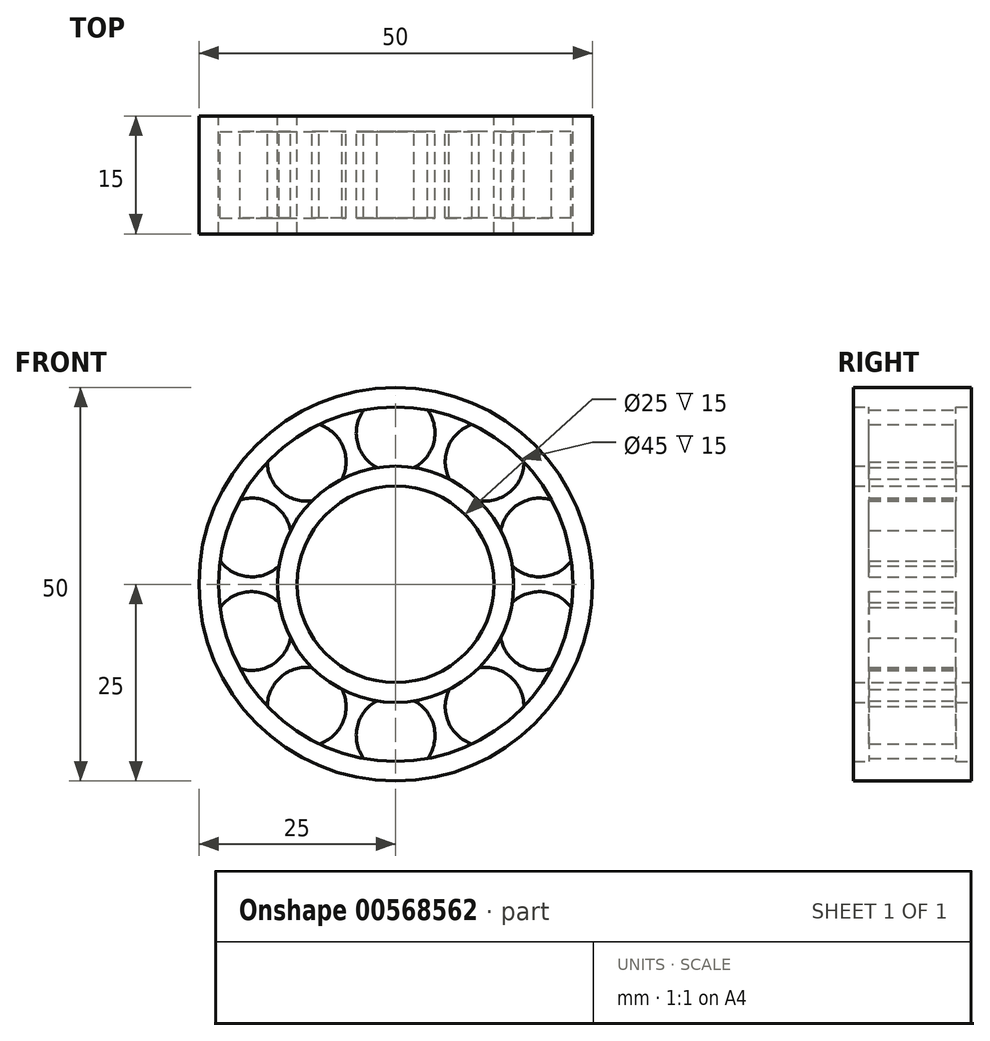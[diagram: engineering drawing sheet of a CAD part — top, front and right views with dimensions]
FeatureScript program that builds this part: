
annotation { "Feature Type Name" : "Feature", "Feature Type Description" : "" }
export const myFeature = defineFeature(function(context is Context, id is Id, definition is map)
    precondition{}
    {
        {
            var Q0;
            Q0=qCreatedBy(makeId("Front.planeOp"),FACE);
            cPlane(context, id + "F0", {"entities" : qUnion([Q0]), "cplaneType" : CPlaneType.OFFSET, "offset" : 2 * mm, "width" : 150 * mm, "height" : 150 * mm});
        }
        {
            var Q0;
            Q0=qCreatedBy(makeId("Front.planeOp"),FACE);
            var sketch = newSketch(context, id + "F1", { "sketchPlane" : qUnion([Q0])});
            skCircle(sketch, "E0", {"center": v(0, 0) * mm, "radius": 12.5 * mm});
            skCircle(sketch, "E1", {"center": v(0, 0) * mm, "radius": 15 * mm});
            skCircle(sketch, "E2", {"center": v(0, 0) * mm, "radius": 22.5 * mm});
            skCircle(sketch, "E3", {"center": v(0, 0) * mm, "radius": 25 * mm});
            skSolve(sketch);
        }
        {
            var Q0;
            Q0=makeQuery(id+"F1.imprint","IMPRINT",FACE,{"disambiguationData":[TD([[makeQuery(id+"F1.imprint","IMPRINT",EDGE,{"derivedFrom":sQuery(id+"F1.wireOp",EDGE,"E2")}),-1.0]])]});
            var Q1;
            Q1=makeQuery(id+"F1.imprint","IMPRINT",FACE,{"disambiguationData":[TD([[makeQuery(id+"F1.imprint","IMPRINT",EDGE,{"derivedFrom":sQuery(id+"F1.wireOp",EDGE,"E0")}),-1.0]])]});
            extrude(context, id + "F2", {"entities" : qUnion([Q0, Q1]), "depth" : 15 * mm, "offsetDistance" : 25 * mm});
        }
        {
            var Q0;
            Q0=qCreatedBy(id+"F0.planeOp",FACE);
            var sketch = newSketch(context, id + "F3", { "sketchPlane" : qUnion([Q0])});
            skCircle(sketch, "E4", {"center": v(0, 19.22) * mm, "radius": 5 * mm});
            skCircle(sketch, "E5.1.0", {"center": v(-11.3, 15.55) * mm, "radius": 5 * mm});
            skCircle(sketch, "E5.2.0", {"center": v(-18.28, 5.94) * mm, "radius": 5 * mm});
            skCircle(sketch, "E5.3.0", {"center": v(-18.28, -5.94) * mm, "radius": 5 * mm});
            skCircle(sketch, "E5.4.0", {"center": v(-11.3, -15.55) * mm, "radius": 5 * mm});
            skCircle(sketch, "E5.5.0", {"center": v(0, -19.22) * mm, "radius": 5 * mm});
            skCircle(sketch, "E5.6.0", {"center": v(11.3, -15.55) * mm, "radius": 5 * mm});
            skCircle(sketch, "E5.7.0", {"center": v(18.28, -5.94) * mm, "radius": 5 * mm});
            skCircle(sketch, "E5.8.0", {"center": v(18.28, 5.94) * mm, "radius": 5 * mm});
            skCircle(sketch, "E5.9.0", {"center": v(11.3, 15.55) * mm, "radius": 5 * mm});
            skPoint(sketch, "E5.center", {"position": v(0, 0) * mm});
            skSolve(sketch);
        }
        {
            var Q0;
            Q0=makeQuery(id+"F3.imprint","IMPRINT",FACE,{"disambiguationData":[TD([[makeQuery(id+"F3.imprint","IMPRINT",EDGE,{"derivedFrom":sQuery(id+"F3.wireOp",EDGE,"E4")}),1.0]])]});
            var Q1;
            Q1=makeQuery(id+"F3.imprint","IMPRINT",FACE,{"disambiguationData":[TD([[makeQuery(id+"F3.imprint","IMPRINT",EDGE,{"derivedFrom":sQuery(id+"F3.wireOp",EDGE,"E5.1.0")}),1.0]])]});
            var Q2;
            Q2=makeQuery(id+"F3.imprint","IMPRINT",FACE,{"disambiguationData":[TD([[makeQuery(id+"F3.imprint","IMPRINT",EDGE,{"derivedFrom":sQuery(id+"F3.wireOp",EDGE,"E5.2.0")}),1.0]])]});
            var Q3;
            Q3=makeQuery(id+"F3.imprint","IMPRINT",FACE,{"disambiguationData":[TD([[makeQuery(id+"F3.imprint","IMPRINT",EDGE,{"derivedFrom":sQuery(id+"F3.wireOp",EDGE,"E5.3.0")}),1.0]])]});
            var Q4;
            Q4=makeQuery(id+"F3.imprint","IMPRINT",FACE,{"disambiguationData":[TD([[makeQuery(id+"F3.imprint","IMPRINT",EDGE,{"derivedFrom":sQuery(id+"F3.wireOp",EDGE,"E5.4.0")}),1.0]])]});
            var Q5;
            Q5=makeQuery(id+"F3.imprint","IMPRINT",FACE,{"disambiguationData":[TD([[makeQuery(id+"F3.imprint","IMPRINT",EDGE,{"derivedFrom":sQuery(id+"F3.wireOp",EDGE,"E5.5.0")}),1.0]])]});
            var Q6;
            Q6=makeQuery(id+"F3.imprint","IMPRINT",FACE,{"disambiguationData":[TD([[makeQuery(id+"F3.imprint","IMPRINT",EDGE,{"derivedFrom":sQuery(id+"F3.wireOp",EDGE,"E5.6.0")}),1.0]])]});
            var Q7;
            Q7=makeQuery(id+"F3.imprint","IMPRINT",FACE,{"disambiguationData":[TD([[makeQuery(id+"F3.imprint","IMPRINT",EDGE,{"derivedFrom":sQuery(id+"F3.wireOp",EDGE,"E5.7.0")}),1.0]])]});
            var Q8;
            Q8=makeQuery(id+"F3.imprint","IMPRINT",FACE,{"disambiguationData":[TD([[makeQuery(id+"F3.imprint","IMPRINT",EDGE,{"derivedFrom":sQuery(id+"F3.wireOp",EDGE,"E5.8.0")}),1.0]])]});
            var Q9;
            Q9=makeQuery(id+"F3.imprint","IMPRINT",FACE,{"disambiguationData":[TD([[makeQuery(id+"F3.imprint","IMPRINT",EDGE,{"derivedFrom":sQuery(id+"F3.wireOp",EDGE,"E5.9.0")}),1.0]])]});
            extrude(context, id + "F4", {"entities" : qUnion([Q0, Q1, Q2, Q3, Q4, Q5, Q6, Q7, Q8, Q9]), "operationType" : NewBodyOperationType.ADD, "depth" : 11 * mm, "offsetDistance" : 25 * mm});
        }
    });
